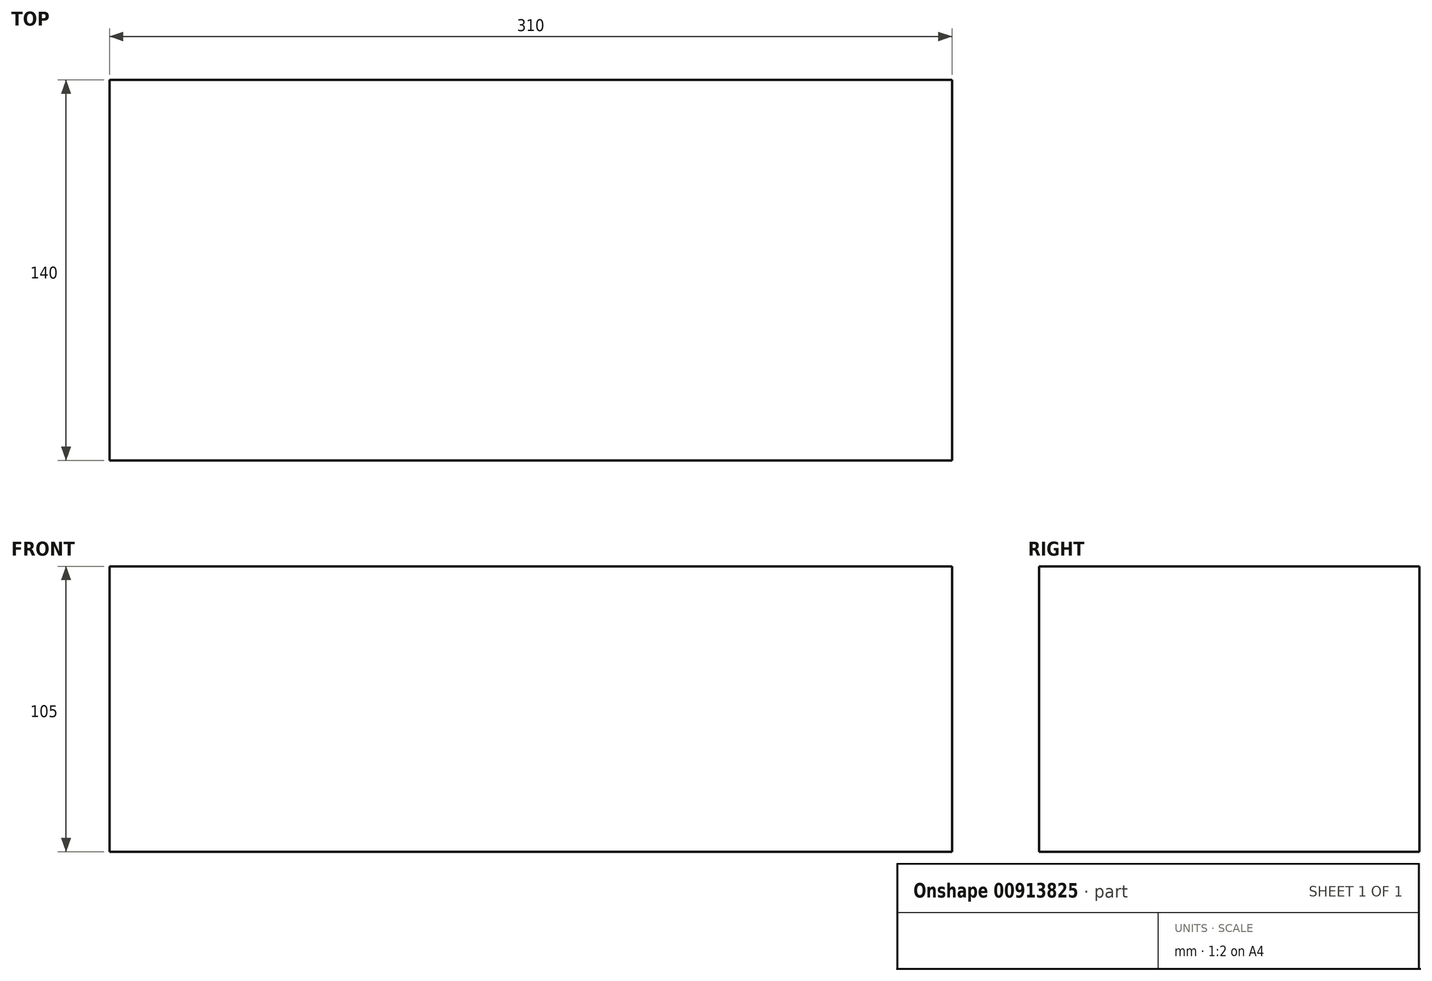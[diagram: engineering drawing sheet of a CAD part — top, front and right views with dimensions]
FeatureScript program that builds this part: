
annotation { "Feature Type Name" : "Feature", "Feature Type Description" : "" }
export const myFeature = defineFeature(function(context is Context, id is Id, definition is map)
    precondition{}
    {
        {
            var Q0;
            Q0=qCreatedBy(makeId("Top.planeOp"),FACE);
            var sketch = newSketch(context, id + "F0", { "sketchPlane" : qUnion([Q0])});
            skLineSegment(sketch, "E0.bottom", {"start": v(155, -70) * mm, "end": v(-155, -70) * mm});
            skLineSegment(sketch, "E0.top", {"start": v(155, 70) * mm, "end": v(-155, 70) * mm});
            skLineSegment(sketch, "E0.left", {"start": v(155, -70) * mm, "end": v(155, 70) * mm});
            skLineSegment(sketch, "E0.right", {"start": v(-155, -70) * mm, "end": v(-155, 70) * mm});
            skPoint(sketch, "E0.middle", {"position": v(0, 0) * mm});
            skSolve(sketch);
        }
        {
            var Q0;
            Q0=makeQuery(id+"F0.imprint","IMPRINT",FACE,{"disambiguationData":[TD([[makeQuery(id+"F0.imprint","IMPRINT",EDGE,{"derivedFrom":sQuery(id+"F0.wireOp",EDGE,"E0.bottom")}),-1.0]])]});
            extrude(context, id + "F1", {"entities" : qUnion([Q0]), "depth" : 105 * mm, "offsetDistance" : 25 * mm});
        }
    });
